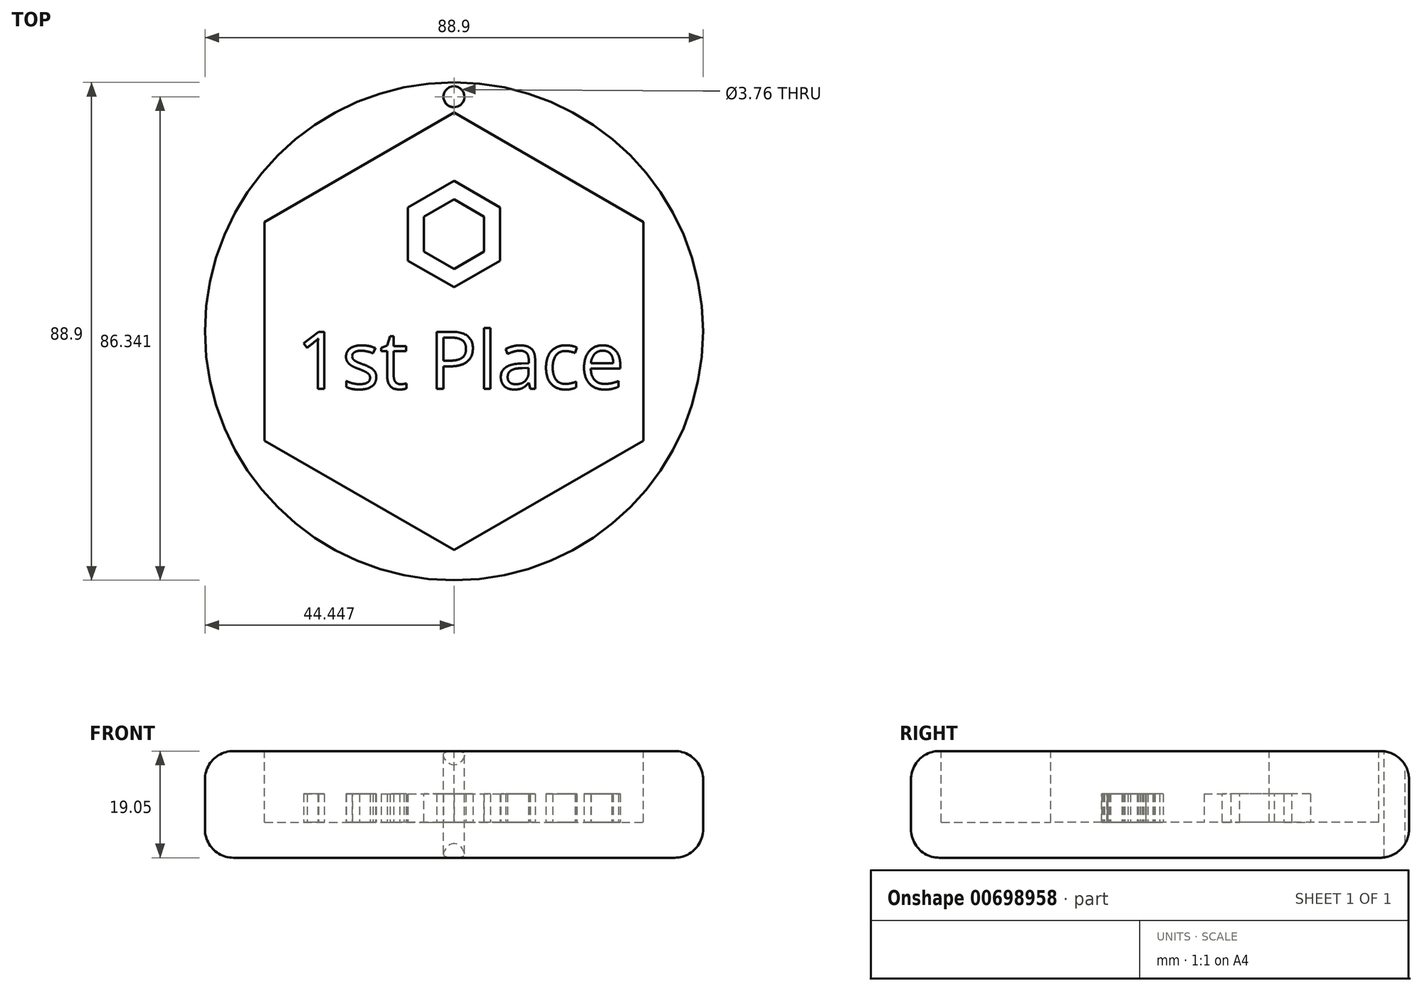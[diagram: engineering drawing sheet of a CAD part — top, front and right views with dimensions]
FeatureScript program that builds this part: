
annotation { "Feature Type Name" : "Feature", "Feature Type Description" : "" }
export const myFeature = defineFeature(function(context is Context, id is Id, definition is map)
    precondition{}
    {
        {
            var Q0;
            Q0=qCreatedBy(makeId("Top.planeOp"),FACE);
            var sketch = newSketch(context, id + "F0", { "sketchPlane" : qUnion([Q0])});
            skCircle(sketch, "E0", {"center": v(0, 0) * mm, "radius": 44.45 * mm});
            skSolve(sketch);
        }
        {
            var Q0;
            Q0=makeQuery(id+"F0.imprint","IMPRINT",FACE,{"disambiguationData":[TD([[makeQuery(id+"F0.imprint","IMPRINT",EDGE,{"derivedFrom":sQuery(id+"F0.wireOp",EDGE,"E0")}),1.0]])]});
            extrude(context, id + "F1", {"entities" : qUnion([Q0]), "depth" : 19.05 * mm, "offsetDistance" : 25.4 * mm});
        }
        {
            var Q0;
            Q0=makeQuery(id+"F1.opExtrude","CAP_FACE",FACE,{"disambiguationData":[OSD([sQuery(id+"F0.wireOp",EDGE,"E0")])],"isStart":false});
            var sketch = newSketch(context, id + "F2", { "sketchPlane" : qUnion([Q0])});
            skCircle(sketch, "E1.cCircle", {"center": v(0, 0) * mm, "radius": 33.81 * mm, "construction": true});
            skLineSegment(sketch, "E1.0", {"start": v(33.81, 19.52) * mm, "end": v(33.81, -19.52) * mm});
            skLineSegment(sketch, "E1.1", {"start": v(33.81, -19.52) * mm, "end": v(0, -39.04) * mm});
            skLineSegment(sketch, "E1.2", {"start": v(0, -39.04) * mm, "end": v(-33.81, -19.52) * mm});
            skLineSegment(sketch, "E1.3", {"start": v(-33.81, -19.52) * mm, "end": v(-33.81, 19.52) * mm});
            skLineSegment(sketch, "E1.4", {"start": v(-33.81, 19.52) * mm, "end": v(0, 39.04) * mm});
            skLineSegment(sketch, "E1.5", {"start": v(0, 39.04) * mm, "end": v(33.81, 19.52) * mm});
            skPoint(sketch, "E1.0.midPoint", {"position": v(33.81, 0) * mm});
            skSolve(sketch);
        }
        {
            var Q0;
            Q0=makeQuery(id+"F2.imprint","IMPRINT",FACE,{"disambiguationData":[TD([[makeQuery(id+"F2.imprint","IMPRINT",EDGE,{"derivedFrom":sQuery(id+"F2.wireOp",EDGE,"E1.0")}),-1.0]])]});
            extrude(context, id + "F3", {"entities" : qUnion([Q0]), "operationType" : NewBodyOperationType.REMOVE, "oppositeDirection" : true, "depth" : 12.7 * mm, "offsetDistance" : 25.4 * mm});
        }
        {
            var Q0;
            Q0=makeQuery(id+"F1.opExtrude","CAP_FACE",FACE,{"disambiguationData":[OSD([sQuery(id+"F0.wireOp",EDGE,"E0")])],"isStart":false});
            var sketch = newSketch(context, id + "F4", { "sketchPlane" : qUnion([Q0])});
            skCircle(sketch, "E2", {"center": v(0, 41.9) * mm, "radius": 1.88 * mm});
            skSolve(sketch);
        }
        {
            var Q0;
            Q0=makeQuery(id+"F4.imprint","IMPRINT",FACE,{"disambiguationData":[TD([[makeQuery(id+"F4.imprint","IMPRINT",EDGE,{"derivedFrom":sQuery(id+"F4.wireOp",EDGE,"E2")}),1.0]])]});
            extrude(context, id + "F5", {"entities" : qUnion([Q0]), "operationType" : NewBodyOperationType.REMOVE, "oppositeDirection" : true, "depth" : 40.5 * mm, "offsetDistance" : 25.4 * mm});
        }
        {
            var Q0;
            Q0=makeQuery(id+"F3.boolean.opBoolean","COPY",FACE,{"derivedFrom":makeQuery(id+"F3.opExtrude","CAP_FACE",FACE,{"disambiguationData":[OSD([sQuery(id+"F2.wireOp",EDGE,"E1.0"),sQuery(id+"F2.wireOp",EDGE,"E1.1"),sQuery(id+"F2.wireOp",EDGE,"E1.2"),sQuery(id+"F2.wireOp",EDGE,"E1.3"),sQuery(id+"F2.wireOp",EDGE,"E1.4"),sQuery(id+"F2.wireOp",EDGE,"E1.5")])],"isStart":false})});
            var sketch = newSketch(context, id + "F6", { "sketchPlane" : qUnion([Q0])});
            skText(sketch, "E3", { "text": "1st Place", "fontName": "OpenSans-Regular.ttf"});
            const initialGuessF6  = {"E3": [-0.02816, -0.01026, 1, 0, 0.01026]};
            skSetInitialGuess(sketch, initialGuessF6);
            skSolve(sketch);
        }
        {
            var Q0;
            Q0 = qSketchRegion(id + "F6", true);
            extrude(context, id + "F7", {"entities" : qUnion([Q0]), "operationType" : NewBodyOperationType.ADD, "depth" : 5.08 * mm, "offsetDistance" : 25.4 * mm});
        }
        {
            var Q0;
            {var subQ0=sQuery(id+"F2.wireOp",EDGE,"E1.5");var subQ1=sQuery(id+"F2.wireOp",EDGE,"E1.4");var subQ2=sQuery(id+"F2.wireOp",EDGE,"E1.3");var subQ3=sQuery(id+"F2.wireOp",EDGE,"E1.2");var subQ4=sQuery(id+"F2.wireOp",EDGE,"E1.1");var subQ5=sQuery(id+"F2.wireOp",EDGE,"E1.0");Q0=makeQuery(id+"F7.boolean.opBoolean","SPLIT",FACE,{"disambiguationData":[TD([makeQuery(id+"F3.boolean.opBoolean","COPY",FACE,{"derivedFrom":makeQuery(id+"F3.opExtrude","SWEPT_FACE",FACE,{"disambiguationData":[OSD([subQ5])]})})])],"derivedFrom":makeQuery(id+"F3.boolean.opBoolean","COPY",FACE,{"derivedFrom":makeQuery(id+"F3.opExtrude","CAP_FACE",FACE,{"disambiguationData":[OSD([subQ5,subQ4,subQ3,subQ2,subQ1,subQ0])],"isStart":false})})});}
            var sketch = newSketch(context, id + "F8", { "sketchPlane" : qUnion([Q0])});
            skCircle(sketch, "E4.cCircle", {"center": v(0, 17.36) * mm, "radius": 8.22 * mm, "construction": true});
            skLineSegment(sketch, "E4.0", {"start": v(8.22, 22.11) * mm, "end": v(8.22, 12.61) * mm});
            skLineSegment(sketch, "E4.1", {"start": v(8.22, 12.61) * mm, "end": v(0, 7.87) * mm});
            skLineSegment(sketch, "E4.2", {"start": v(0, 7.87) * mm, "end": v(-8.22, 12.61) * mm});
            skLineSegment(sketch, "E4.3", {"start": v(-8.22, 12.61) * mm, "end": v(-8.22, 22.11) * mm});
            skLineSegment(sketch, "E4.4", {"start": v(-8.22, 22.11) * mm, "end": v(0, 26.86) * mm});
            skLineSegment(sketch, "E4.5", {"start": v(0, 26.86) * mm, "end": v(8.22, 22.11) * mm});
            skPoint(sketch, "E4.0.midPoint", {"position": v(8.22, 17.36) * mm});
            skSolve(sketch);
        }
        {
            var Q0;
            Q0=makeQuery(id+"F8.imprint","IMPRINT",FACE,{"disambiguationData":[TD([[makeQuery(id+"F8.imprint","IMPRINT",EDGE,{"derivedFrom":sQuery(id+"F8.wireOp",EDGE,"E4.0")}),-1.0]])]});
            extrude(context, id + "F9", {"entities" : qUnion([Q0]), "operationType" : NewBodyOperationType.ADD, "depth" : 5.08 * mm, "offsetDistance" : 25.4 * mm});
        }
        {
            var Q0;
            Q0=makeQuery(id+"F9.opExtrude","CAP_FACE",FACE,{"disambiguationData":[OSD([sQuery(id+"F8.wireOp",EDGE,"E4.0"),sQuery(id+"F8.wireOp",EDGE,"E4.1"),sQuery(id+"F8.wireOp",EDGE,"E4.2"),sQuery(id+"F8.wireOp",EDGE,"E4.3"),sQuery(id+"F8.wireOp",EDGE,"E4.4"),sQuery(id+"F8.wireOp",EDGE,"E4.5")])],"isStart":false});
            var sketch = newSketch(context, id + "F10", { "sketchPlane" : qUnion([Q0])});
            skCircle(sketch, "E5.cCircle", {"center": v(0, 17.36) * mm, "radius": 5.38 * mm, "construction": true});
            skPoint(sketch, "E5.cCircle.centerSnap0", {"position": v(-8.22, 17.36) * mm});
            skLineSegment(sketch, "E5.0", {"start": v(5.38, 20.47) * mm, "end": v(5.38, 14.26) * mm});
            skLineSegment(sketch, "E5.1", {"start": v(5.38, 14.26) * mm, "end": v(0, 11.15) * mm});
            skLineSegment(sketch, "E5.2", {"start": v(0, 11.15) * mm, "end": v(-5.38, 14.26) * mm});
            skLineSegment(sketch, "E5.3", {"start": v(-5.38, 14.26) * mm, "end": v(-5.38, 20.47) * mm});
            skLineSegment(sketch, "E5.4", {"start": v(-5.38, 20.47) * mm, "end": v(0, 23.58) * mm});
            skLineSegment(sketch, "E5.5", {"start": v(0, 23.58) * mm, "end": v(5.38, 20.47) * mm});
            skPoint(sketch, "E5.0.midPoint", {"position": v(5.38, 17.36) * mm});
            skSolve(sketch);
        }
        {
            var Q0;
            Q0=makeQuery(id+"F10.imprint","IMPRINT",FACE,{"disambiguationData":[TD([[makeQuery(id+"F10.imprint","IMPRINT",EDGE,{"derivedFrom":sQuery(id+"F10.wireOp",EDGE,"E5.0")}),-1.0]])]});
            extrude(context, id + "F11", {"entities" : qUnion([Q0]), "operationType" : NewBodyOperationType.REMOVE, "oppositeDirection" : true, "depth" : 5.08 * mm, "offsetDistance" : 25.4 * mm});
        }
        {
            var Q0;
            Q0=makeQuery(id+"F1.opExtrude","CAP_EDGE",EDGE,{"disambiguationData":[OSD([sQuery(id+"F0.wireOp",EDGE,"E0")])],"isStart":false});
            var Q1;
            Q1=makeQuery(id+"F1.opExtrude","CAP_EDGE",EDGE,{"disambiguationData":[OSD([sQuery(id+"F0.wireOp",EDGE,"E0")])],"isStart":true});
            fillet(context, id + "F12", {"entities" : qUnion([Q0, Q1]), "radius" : 5.08 * mm, "tangentPropagation" : true, "allowEdgeOverflow" : false});
        }
    });
